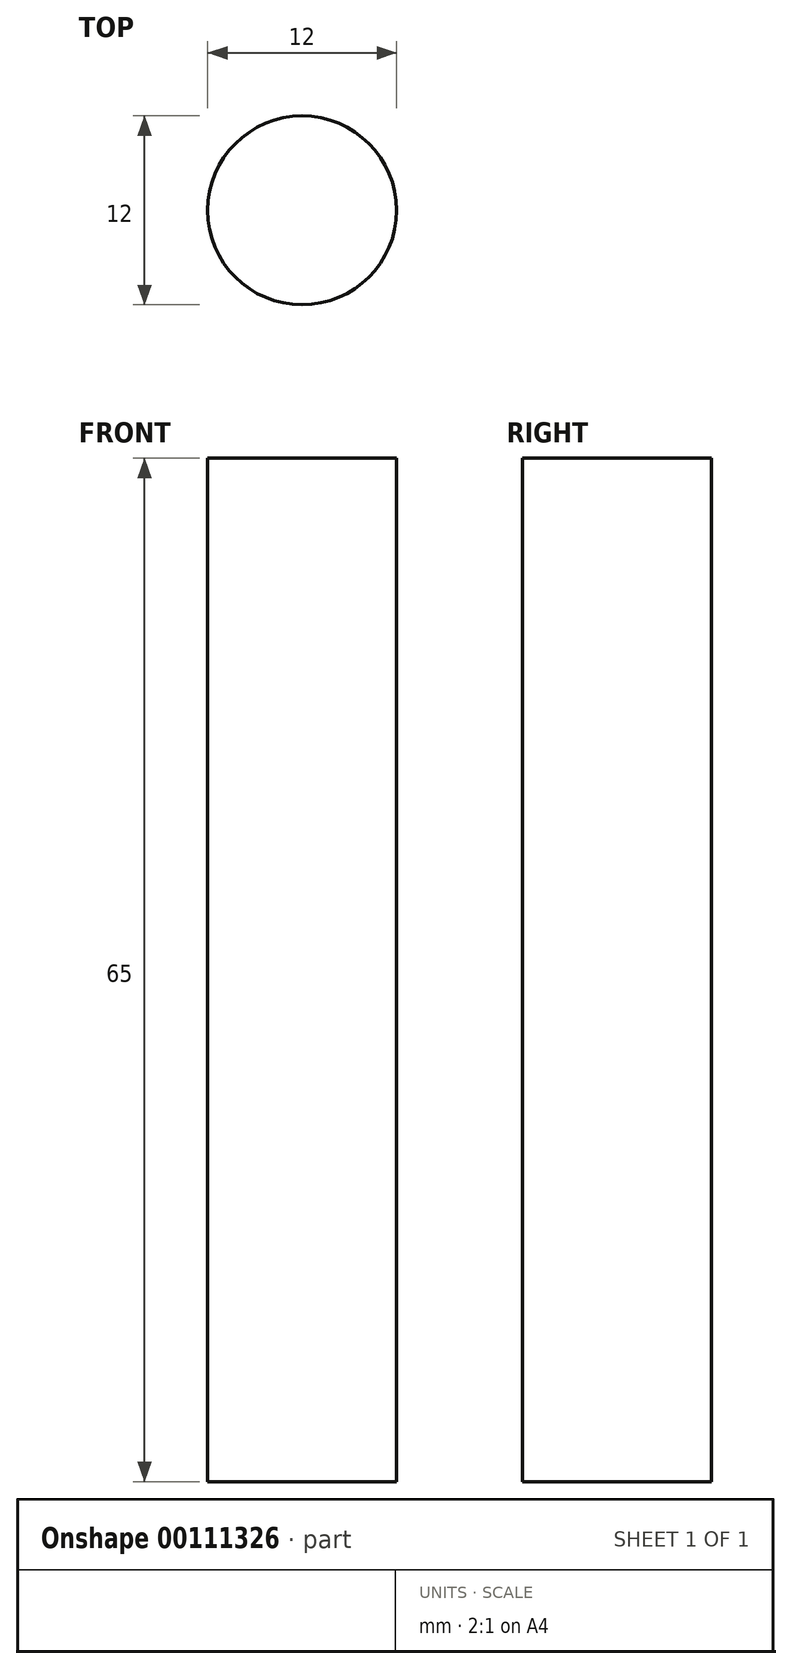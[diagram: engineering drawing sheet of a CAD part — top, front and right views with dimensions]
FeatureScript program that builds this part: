
annotation { "Feature Type Name" : "Feature", "Feature Type Description" : "" }
export const myFeature = defineFeature(function(context is Context, id is Id, definition is map)
    precondition{}
    {
        {
            var Q0;
            Q0=qCreatedBy(makeId("Top.planeOp"),FACE);
            var sketch = newSketch(context, id + "F0", { "sketchPlane" : qUnion([Q0])});
            skCircle(sketch, "E0", {"center": v(0, 0) * mm, "radius": 6 * mm});
            skSolve(sketch);
        }
        {
            var Q0;
            Q0=qSketchRegion(id+"F0",true);
            extrude(context, id + "F1", {"entities" : qUnion([Q0]), "depth" : 65 * mm});
        }
    });
